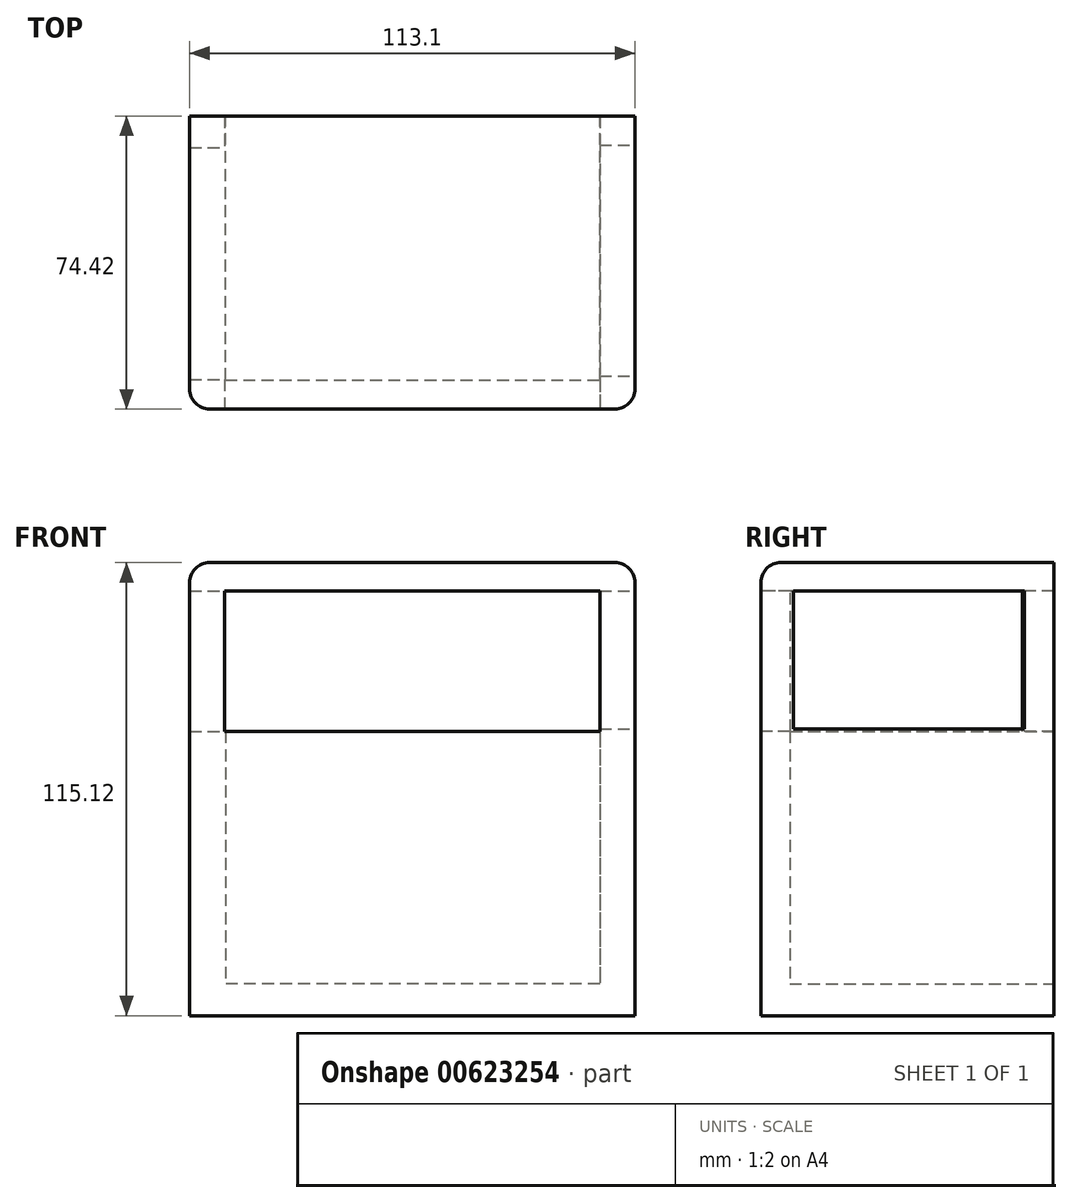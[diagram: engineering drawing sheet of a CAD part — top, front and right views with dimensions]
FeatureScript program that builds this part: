
annotation { "Feature Type Name" : "Feature", "Feature Type Description" : "" }
export const myFeature = defineFeature(function(context is Context, id is Id, definition is map)
    precondition{}
    {
        {
            var Q0;
            Q0=qCreatedBy(makeId("Front.planeOp"),FACE);
            var sketch = newSketch(context, id + "F0", { "sketchPlane" : qUnion([Q0])});
            skLineSegment(sketch, "E0.bottom", {"start": v(-50.65, 61.16) * mm, "end": v(62.45, 61.16) * mm});
            skLineSegment(sketch, "E0.top", {"start": v(-50.65, -53.96) * mm, "end": v(62.45, -53.96) * mm});
            skLineSegment(sketch, "E0.left", {"start": v(-50.65, 61.16) * mm, "end": v(-50.65, -53.96) * mm});
            skLineSegment(sketch, "E0.right", {"start": v(62.45, 61.16) * mm, "end": v(62.45, -53.96) * mm});
            skSolve(sketch);
        }
        {
            var Q0;
            Q0=makeQuery(id+"F0.imprint","IMPRINT",FACE,{"disambiguationData":[TD([[makeQuery(id+"F0.imprint","IMPRINT",EDGE,{"derivedFrom":sQuery(id+"F0.wireOp",EDGE,"E0.bottom")}),-1.0]])]});
            var Q1;
            Q1=sQuery(id+"F0.wireOp",EDGE,"E0.left");
            var Q2;
            Q2=sQuery(id+"F0.wireOp",EDGE,"E0.bottom");
            var Q3;
            Q3=sQuery(id+"F0.wireOp",EDGE,"E0.right");
            var Q4;
            Q4=sQuery(id+"F0.wireOp",EDGE,"E0.top");
            extrude(context, id + "F1", {"entities" : qUnion([Q0]), "surfaceEntities" : qUnion([Q1, Q2, Q3, Q4]), "oppositeDirection" : true, "depth" : 74.42 * mm, "offsetDistance" : 25.4 * mm});
        }
        {
            var Q0;
            Q0=qCreatedBy(makeId("Front.planeOp"),FACE);
            var sketch = newSketch(context, id + "F2", { "sketchPlane" : qUnion([Q0])});
            skLineSegment(sketch, "E1.bottom", {"start": v(-41.73, 53.96) * mm, "end": v(53.53, 53.96) * mm});
            skLineSegment(sketch, "E1.top", {"start": v(-41.73, 18.28) * mm, "end": v(53.53, 18.28) * mm});
            skLineSegment(sketch, "E1.left", {"start": v(-41.73, 53.96) * mm, "end": v(-41.73, 18.28) * mm});
            skLineSegment(sketch, "E1.right", {"start": v(53.53, 53.96) * mm, "end": v(53.53, 18.28) * mm});
            skSolve(sketch);
        }
        {
            var Q0;
            Q0=makeQuery(id+"F2.imprint","IMPRINT",FACE,{"disambiguationData":[TD([[makeQuery(id+"F2.imprint","IMPRINT",EDGE,{"derivedFrom":sQuery(id+"F2.wireOp",EDGE,"E1.bottom")}),-1.0]])]});
            extrude(context, id + "F3", {"entities" : qUnion([Q0]), "operationType" : NewBodyOperationType.REMOVE, "oppositeDirection" : true, "depth" : 127.76 * mm, "offsetDistance" : 25.4 * mm});
        }
        {
            var Q0;
            Q0=qCreatedBy(makeId("Right.planeOp"),FACE);
            var sketch = newSketch(context, id + "F4", { "sketchPlane" : qUnion([Q0])});
            skLineSegment(sketch, "E2.bottom", {"start": v(66.4, 53.96) * mm, "end": v(7.53, 53.96) * mm});
            skLineSegment(sketch, "E2.top", {"start": v(66.4, 18.28) * mm, "end": v(7.53, 18.28) * mm});
            skLineSegment(sketch, "E2.left", {"start": v(66.4, 53.96) * mm, "end": v(66.4, 18.28) * mm});
            skLineSegment(sketch, "E2.right", {"start": v(7.53, 53.96) * mm, "end": v(7.53, 18.28) * mm});
            skSolve(sketch);
        }
        {
            var Q0;
            Q0=makeQuery(id+"F4.imprint","IMPRINT",FACE,{"disambiguationData":[TD([[makeQuery(id+"F4.imprint","IMPRINT",EDGE,{"derivedFrom":sQuery(id+"F4.wireOp",EDGE,"E2.bottom")}),1.0]])]});
            extrude(context, id + "F5", {"entities" : qUnion([Q0]), "operationType" : NewBodyOperationType.REMOVE, "oppositeDirection" : true, "depth" : 78.49 * mm, "offsetDistance" : 25.4 * mm});
        }
        {
            var Q0;
            Q0=makeQuery(id+"F1.opExtrude","SWEPT_FACE",FACE,{"disambiguationData":[OSD([sQuery(id+"F0.wireOp",EDGE,"E0.right")])]});
            var sketch = newSketch(context, id + "F6", { "sketchPlane" : qUnion([Q0])});
            skLineSegment(sketch, "E3.bottom", {"start": v(8.33, 53.96) * mm, "end": v(67.02, 53.96) * mm});
            skLineSegment(sketch, "E3.top", {"start": v(8.33, 18.85) * mm, "end": v(67.02, 18.85) * mm});
            skLineSegment(sketch, "E3.left", {"start": v(8.33, 53.96) * mm, "end": v(8.33, 18.85) * mm});
            skLineSegment(sketch, "E3.right", {"start": v(67.02, 53.96) * mm, "end": v(67.02, 18.85) * mm});
            skSolve(sketch);
        }
        {
            var Q0;
            Q0=makeQuery(id+"F6.imprint","IMPRINT",FACE,{"disambiguationData":[TD([[makeQuery(id+"F6.imprint","IMPRINT",EDGE,{"derivedFrom":sQuery(id+"F6.wireOp",EDGE,"E3.bottom")}),-1.0]])]});
            extrude(context, id + "F7", {"entities" : qUnion([Q0]), "operationType" : NewBodyOperationType.REMOVE, "oppositeDirection" : true, "depth" : 72.9 * mm, "offsetDistance" : 25.4 * mm});
        }
        {
            var Q0;
            Q0=makeQuery(id+"F1.opExtrude","CAP_FACE",FACE,{"disambiguationData":[OSD([sQuery(id+"F0.wireOp",EDGE,"E0.bottom"),sQuery(id+"F0.wireOp",EDGE,"E0.top"),sQuery(id+"F0.wireOp",EDGE,"E0.left"),sQuery(id+"F0.wireOp",EDGE,"E0.right")])],"isStart":false});
            var sketch = newSketch(context, id + "F8", { "sketchPlane" : qUnion([Q0])});
            skLineSegment(sketch, "E4.bottom", {"start": v(-53.53, 18.28) * mm, "end": v(41.59, 18.28) * mm});
            skLineSegment(sketch, "E4.top", {"start": v(-53.53, -45.9) * mm, "end": v(41.59, -45.9) * mm});
            skLineSegment(sketch, "E4.left", {"start": v(-53.53, 18.28) * mm, "end": v(-53.53, -45.9) * mm});
            skLineSegment(sketch, "E4.right", {"start": v(41.59, 18.28) * mm, "end": v(41.59, -45.9) * mm});
            skSolve(sketch);
        }
        {
            var Q0;
            Q0 = qSketchRegion(id + "F8", true);
            extrude(context, id + "F9", {"entities" : qUnion([Q0]), "operationType" : NewBodyOperationType.REMOVE, "oppositeDirection" : true, "depth" : 67.06 * mm, "offsetDistance" : 25.4 * mm});
        }
        {
            var Q0;
            Q0=makeQuery(id+"F1.opExtrude","CAP_EDGE",EDGE,{"disambiguationData":[OSD([sQuery(id+"F0.wireOp",EDGE,"E0.left")])],"isStart":true});
            fillet(context, id + "F10", {"entities" : qUnion([Q0]), "radius" : 5.08 * mm, "tangentPropagation" : true, "allowEdgeOverflow" : false});
        }
        {
            var Q0;
            Q0=makeQuery(id+"F1.opExtrude","CAP_EDGE",EDGE,{"disambiguationData":[OSD([sQuery(id+"F0.wireOp",EDGE,"E0.right")])],"isStart":true});
            var Q1;
            Q1=makeQuery(id+"F1.opExtrude","CAP_EDGE",EDGE,{"disambiguationData":[OSD([sQuery(id+"F0.wireOp",EDGE,"E0.bottom")])],"isStart":true});
            var Q2;
            Q2=makeQuery(id+"F1.opExtrude","SWEPT_EDGE",EDGE,{"disambiguationData":[OSD([sQuery(id+"F0.wireOp",EDGE,"E0.bottom"),sQuery(id+"F0.wireOp",EDGE,"E0.right")])]});
            fillet(context, id + "F11", {"entities" : qUnion([Q0, Q1, Q2]), "radius" : 5.08 * mm, "tangentPropagation" : true, "allowEdgeOverflow" : false});
        }
    });
